# Revit family: 6kt.Schraube DIN EN ISO 4017
name_source: partatom
category: HLS-Bauteile
revit_build: Autodesk Revit 2017 (Build: 20190507_1515(x64)
units: mm (PartAtom-declared; Revit-internal decimal feet)

## family parameters
Arbeitsebenenbasiert = Ja
Beim Laden mit Abzugskörper schneiden = Nein
Bemaßung runder Anschluss = Durchmesser verwenden
Gemeinsam genutzt = Ja
Immer vertikal = Nein
Raumberechnungspunkt = Nein
Teiletyp = Normal

## types (26) — shared parameters
Fabrikat = MEFA
Festigkeitsklasse = 8.8
Firma = MEFA Befestigungs- und Montagesysteme GmbH
Form Kopf = Sechskantkopf
Kurztext1 = Sechskantschraube EN ISO 4017
Material = Stahl
Mengeneinheit = St
Oberflaeche = galvanisch verzinkt
Vorgabe-Ansicht = 1219 mm
vpe = 100 St

## per-type parameters (varying)
| type | Artikelnummer | EAN | Gewicht | Gewicht pro Bauteil | Gewinde | H | Kurztext2 | L | Länge | R | Schlüsselweite | d2 |
| 6kt.-Schraube M10x16 | 3205162 | 4250928438003 | 0.02 kg | 0.02 kg | M10 | 6 mm  [stored 0.019685 ft] | M10 x 16 mm gvz FK 8.8 | 16 mm  [stored 0.0524934 ft] | 16 mm  [stored 0.0524934 ft] | 9 mm  [stored 0.0295276 ft] | 17 | 4 mm  [stored 0.0131234 ft] |
| 6kt.-Schraube M8x20 | 3204205 | 4250928437938 | 0.01 kg | 0.01 kg | M8 | 5 mm  [stored 0.0164042 ft] | M8 x 20 mm gvz FK 8.8 | 20 mm  [stored 0.0656168 ft] | 20 mm  [stored 0.0656168 ft] | 7 mm  [stored 0.0229659 ft] | 13 | 3 mm  [stored 0.00984252 ft] |
| 6kt.-Schraube M10x40 | 3205401 | 4250928438058 | 0.04 kg | 0.04 kg | M10 | 6 mm  [stored 0.019685 ft] | M10 x 40 mm gvz FK 8.8 | 40 mm  [stored 0.131234 ft] | 40 mm  [stored 0.131234 ft] | 9 mm  [stored 0.0295276 ft] | 17 | 4 mm  [stored 0.0131234 ft] |
| 6kt.-Schraube M10x25 | 3205251 | 4250928438027 | 0.03 kg | 0.03 kg | M10 | 6 mm  [stored 0.019685 ft] | M10 x 25 mm gvz FK 8.8 | 25 mm  [stored 0.082021 ft] | 25 mm  [stored 0.082021 ft] | 9 mm  [stored 0.0295276 ft] | 17 | 4 mm  [stored 0.0131234 ft] |
| 6kt.-Schraube M10x30 | 3205301 | 4250928438034 | 0.03 kg | 0.03 kg | M10 | 6 mm  [stored 0.019685 ft] | M10 x 30 mm gvz FK 8.8 | 30 mm  [stored 0.0984252 ft] | 30 mm  [stored 0.0984252 ft] | 9 mm  [stored 0.0295276 ft] | 17 | 4 mm  [stored 0.0131234 ft] |
| 6kt.-Schraube M10x35 | 3205302 | 4250928438041 | 0.03 kg | 0.03 kg | M10 | 6 mm  [stored 0.019685 ft] | M10 x 35 mm gvz FK 8.8 | 35 mm  [stored 0.114829 ft] | 35 mm  [stored 0.114829 ft] | 9 mm  [stored 0.0295276 ft] | 17 | 4 mm  [stored 0.0131234 ft] |
| 6kt.-Schraube M10x50 | 3205501 | 4250928438065 | 0.04 kg | 0.04 kg | M10 | 6 mm  [stored 0.019685 ft] | M10 x 50 mm gvz FK 8.8 | 50 mm  [stored 0.164042 ft] | 50 mm  [stored 0.164042 ft] | 9 mm  [stored 0.0295276 ft] | 17 | 4 mm  [stored 0.0131234 ft] |
| 6kt.-Schraube M10x60 | 3206602 | 4250928438126 | 0.05 kg | 0.05 kg | M10 | 6 mm  [stored 0.019685 ft] | M10 x 60 mm gvz FK 8.8 | 60 mm  [stored 0.19685 ft] | 60 mm  [stored 0.19685 ft] | 9 mm  [stored 0.0295276 ft] | 17 | 4 mm  [stored 0.0131234 ft] |
| 6kt.-Schraube M12x20 | 3206205 | 4250928438072 | 0.03 kg | 0.03 kg | M12 | 8 mm  [stored 0.0262467 ft] | M12 x 20 mm gvz FK 8.8 | 20 mm  [stored 0.0656168 ft] | 20 mm  [stored 0.0656168 ft] | 10 mm  [stored 0.0328084 ft] | 19 | 5 mm  [stored 0.0164042 ft] |
| 6kt.-Schraube M12x25 | 3206591 | 4250928438119 | 0.04 kg | 0.04 kg | M12 | 8 mm  [stored 0.0262467 ft] | M12 x 25 mm gvz FK 8.8 | 25 mm  [stored 0.082021 ft] | 25 mm  [stored 0.082021 ft] | 10 mm  [stored 0.0328084 ft] | 19 | 5 mm  [stored 0.0164042 ft] |
| 6kt.-Schraube M12x30 | 3206305 | 4250928438089 | 0.04 kg | 0.04 kg | M12 | 8 mm  [stored 0.0262467 ft] | M12 x 30 mm gvz FK 8.8 | 30 mm  [stored 0.0984252 ft] | 30 mm  [stored 0.0984252 ft] | 10 mm  [stored 0.0328084 ft] | 19 | 5 mm  [stored 0.0164042 ft] |
| 6kt.-Schraube M12x35 | 3206306 | 4250928438096 | 0.05 kg | 0.05 kg | M12 | 8 mm  [stored 0.0262467 ft] | M12 x 35 mm gvz FK 8.8 | 35 mm  [stored 0.114829 ft] | 35 mm  [stored 0.114829 ft] | 10 mm  [stored 0.0328084 ft] | 19 | 5 mm  [stored 0.0164042 ft] |
| 6kt.-Schraube M12x40 | 3206606 | 4250928438133 | 0.05 kg | 0.05 kg | M12 | 8 mm  [stored 0.0262467 ft] | M12 x 40 mm gvz FK 8.8 | 40 mm  [stored 0.131234 ft] | 40 mm  [stored 0.131234 ft] | 10 mm  [stored 0.0328084 ft] | 19 | 5 mm  [stored 0.0164042 ft] |
| 6kt.-Schraube M12x45 | 32066064 | 4250928438140 | 0.06 kg | 0.06 kg | M12 | 8 mm  [stored 0.0262467 ft] | M12 x 45 mm gvz FK 8.8 | 45 mm  [stored 0.147638 ft] | 45 mm  [stored 0.147638 ft] | 10 mm  [stored 0.0328084 ft] | 19 | 5 mm  [stored 0.0164042 ft] |
| 6kt.-Schraube M12x50 | 32066065 | 4250928438157 | 0.06 kg | 0.06 kg | M12 | 8 mm  [stored 0.0262467 ft] | M12 x 50 mm gvz FK 8.8 | 50 mm  [stored 0.164042 ft] | 50 mm  [stored 0.164042 ft] | 10 mm  [stored 0.0328084 ft] | 19 | 5 mm  [stored 0.0164042 ft] |
| 6kt.-Schraube M12x60 | 32066066 | 4250928438164 | 0.07 kg | 0.07 kg | M12 | 8 mm  [stored 0.0262467 ft] | M12 x 60 mm gvz FK 8.8 | 60 mm  [stored 0.19685 ft] | 60 mm  [stored 0.19685 ft] | 10 mm  [stored 0.0328084 ft] | 19 | 5 mm  [stored 0.0164042 ft] |
| 6kt.-Schraube M8x16 | 3204165 | 4250928437921 | 0.01 kg | 0.01 kg | M8 | 5 mm  [stored 0.0164042 ft] | M8 x 16 mm gvz FK 8.8 | 16 mm  [stored 0.0524934 ft] | 16 mm  [stored 0.0524934 ft] | 7 mm  [stored 0.0229659 ft] | 13 | 3 mm  [stored 0.00984252 ft] |
| 6kt.-Schraube M8x25 | 3204255 | 4250928437945 | 0.02 kg | 0.02 kg | M8 | 5 mm  [stored 0.0164042 ft] | M8 x 25 mm gvz FK 8.8 | 25 mm  [stored 0.082021 ft] | 25 mm  [stored 0.082021 ft] | 7 mm  [stored 0.0229659 ft] | 13 | 3 mm  [stored 0.00984252 ft] |
| 6kt.-Schraube M8x30 | 3204305 | 4250928437952 | 0.02 kg | 0.02 kg | M8 | 5 mm  [stored 0.0164042 ft] | M8 x 30 mm gvz FK 8.8 | 30 mm  [stored 0.0984252 ft] | 30 mm  [stored 0.0984252 ft] | 7 mm  [stored 0.0229659 ft] | 13 | 3 mm  [stored 0.00984252 ft] |
| 6kt.-Schraube M8x35 | 3204355 | 4250928437969 | 0.02 kg | 0.02 kg | M8 | 5 mm  [stored 0.0164042 ft] | M8 x 35 mm gvz FK 8.8 | 35 mm  [stored 0.114829 ft] | 35 mm  [stored 0.114829 ft] | 7 mm  [stored 0.0229659 ft] | 13 | 3 mm  [stored 0.00984252 ft] |
| 6kt.-Schraube M8x40 | 3204405 | 4250928437976 | 0.02 kg | 0.02 kg | M8 | 5 mm  [stored 0.0164042 ft] | M8 x 40 mm gvz FK 8.8 | 40 mm  [stored 0.131234 ft] | 40 mm  [stored 0.131234 ft] | 7 mm  [stored 0.0229659 ft] | 13 | 3 mm  [stored 0.00984252 ft] |
| 6kt.-Schraube M8x45 | 3204455 | 4250928437983 | 0.02 kg | 0.02 kg | M8 | 5 mm  [stored 0.0164042 ft] | M8 x 45 mm gvz FK 8.8 | 45 mm  [stored 0.147638 ft] | 45 mm  [stored 0.147638 ft] | 7 mm  [stored 0.0229659 ft] | 13 | 3 mm  [stored 0.00984252 ft] |
| 6kt.-Schraube M8x50 | 3204503 | 4250928437990 | 0.03 kg | 0.03 kg | M8 | 5 mm  [stored 0.0164042 ft] | M8 x 50 mm gvz FK 8.8 | 50 mm  [stored 0.164042 ft] | 50 mm  [stored 0.164042 ft] | 7 mm  [stored 0.0229659 ft] | 13 | 3 mm  [stored 0.00984252 ft] |
| 6kt.-Schraube M10x20 | 3205201 | 4250928438010 | 0.02 kg | 0.02 kg | M10 | 6 mm  [stored 0.019685 ft] | M10 x 20 mm gvz FK 8.8 | 20 mm  [stored 0.0656168 ft] | 20 mm  [stored 0.0656168 ft] | 9 mm  [stored 0.0295276 ft] | 17 | 4 mm  [stored 0.0131234 ft] |
| 6kt.-Schraube M10x45 | 3206508 | 4250928438102 | 0.04 kg | 0.04 kg | M10 | 6 mm  [stored 0.019685 ft] | M10 x 45 mm gvz FK 8.8 | 45 mm  [stored 0.147638 ft] | 45 mm  [stored 0.147638 ft] | 9 mm  [stored 0.0295276 ft] | 17 | 4 mm  [stored 0.0131234 ft] |
| 6kt.-Schraube M12x55 | 320660655 | 4250928449771 | 0.06 kg | 0.06 kg | M12 | 8 mm  [stored 0.0262467 ft] | M12 x 55 mm gvz FK 8.8 | 55 mm  [stored 0.180446 ft] | 55 mm  [stored 0.180446 ft] | 10 mm  [stored 0.0328084 ft] | 19 | 5 mm  [stored 0.0164042 ft] |

note: [stored X ft] marks values corroborated as IEEE doubles in the binary element streams (Revit-internal decimal feet)
